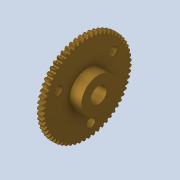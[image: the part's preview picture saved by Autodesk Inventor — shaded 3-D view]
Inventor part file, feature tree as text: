
AUTODESK INVENTOR PART (.ipt)
format: ipt  version: 2020.4 (Build 244396000, 396)  size: 598,528 bytes
history: native  units: mm
features: extrude x2, sketch x2, other x1, pattern_circular x1
ambient origin geometry x8: Origin, YZ Plane, XZ Plane, XY Plane, X Axis, Y Axis, Z Axis, Center Point
bodies: Body1 (feature_tree)
feature tree (6):
  other  "Sólido1"
  extrude  "Thread Entrance"  Depth=1.91mm
  pattern_circular  "Circular Pattern1"  Count=3  [1 undecoded]
  extrude  "Hole Machined"  Depth=10.0mm
  sketch  "Sketch3"  dims[d9=3.0mm d11=1.91mm]
  sketch  "Sketch4"  dims[d12=10.0mm d13=0.0mm d14=30.0mm d15=62.831853mm d17=5.5mm d18=10.0mm d19=0.0mm d20=10.833mm]
note: 1 required parameter value undecoded (feature->parameter linkage not recoverable at this tier; creation-order binding heuristic only, values carry confidence <= 0.55)
